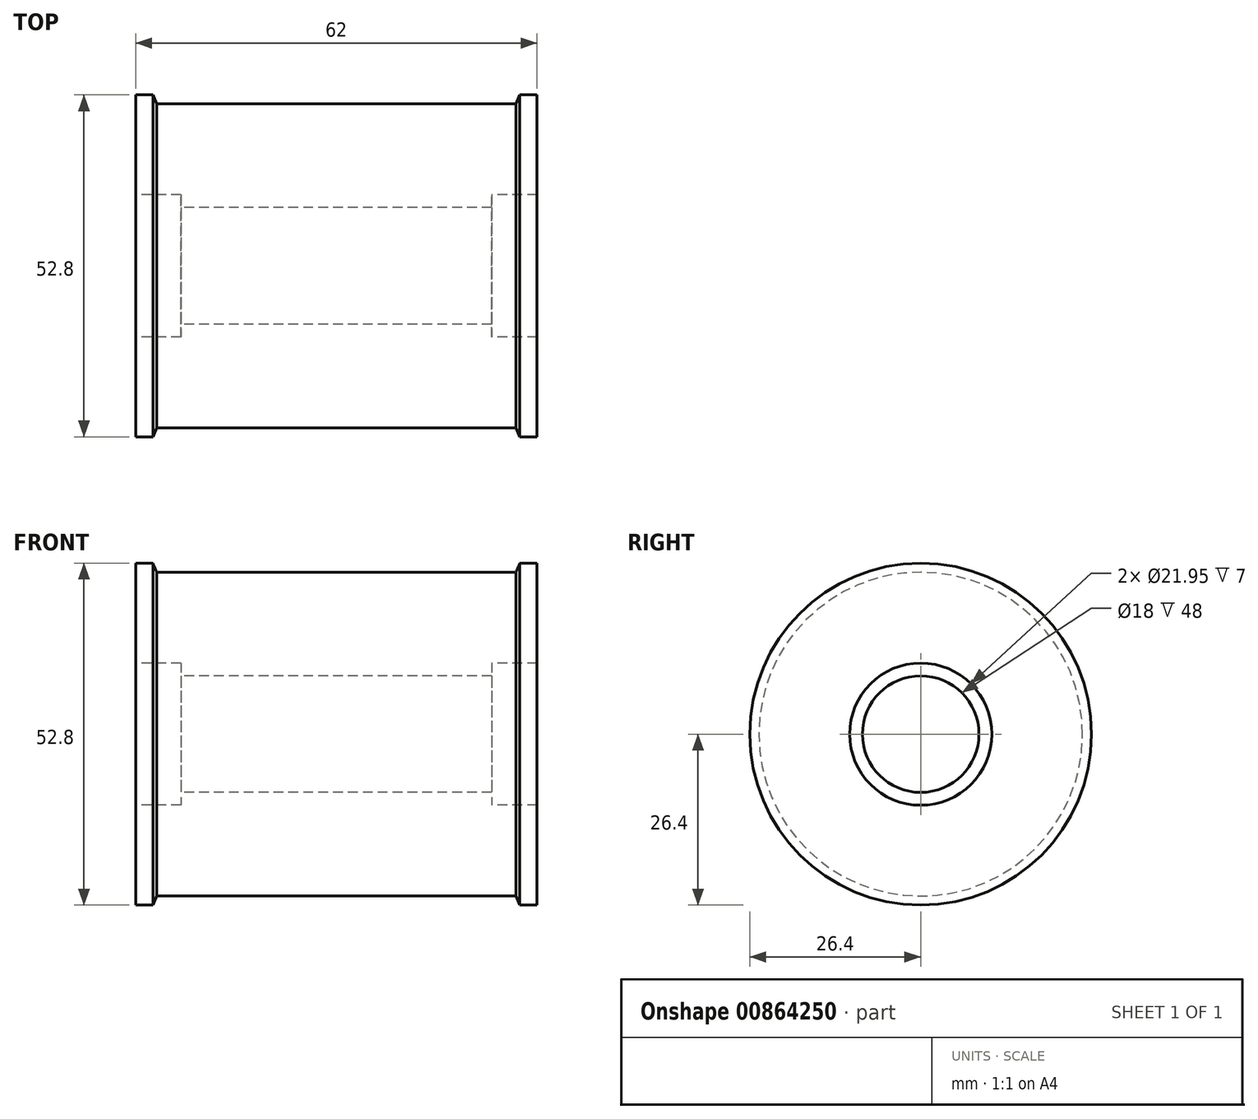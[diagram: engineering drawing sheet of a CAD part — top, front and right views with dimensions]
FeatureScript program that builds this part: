
annotation { "Feature Type Name" : "Feature", "Feature Type Description" : "" }
export const myFeature = defineFeature(function(context is Context, id is Id, definition is map)
    precondition{}
    {
        {
            var Q0;
            Q0=qCreatedBy(makeId("Front.planeOp"),FACE);
            var sketch = newSketch(context, id + "F0", { "sketchPlane" : qUnion([Q0])});
            skLineSegment(sketch, "E0", {"start": v(-4.7, 0) * mm, "end": v(66.37, 0) * mm, "construction": true});
            skLineSegment(sketch, "E1", {"start": v(0, 26.4) * mm, "end": v(0, 10.97) * mm});
            skLineSegment(sketch, "E2", {"start": v(0, 10.97) * mm, "end": v(7, 10.97) * mm});
            skLineSegment(sketch, "E3", {"start": v(7, 10.97) * mm, "end": v(7, 9) * mm});
            skLineSegment(sketch, "E4", {"start": v(7, 9) * mm, "end": v(55, 9) * mm});
            skLineSegment(sketch, "E5", {"start": v(55, 9) * mm, "end": v(55, 10.97) * mm});
            skLineSegment(sketch, "E6", {"start": v(55, 10.97) * mm, "end": v(62, 10.97) * mm});
            skLineSegment(sketch, "E7", {"start": v(62, 10.97) * mm, "end": v(62, 26.4) * mm});
            skLineSegment(sketch, "E8", {"start": v(62, 26.4) * mm, "end": v(59.33, 26.4) * mm});
            skLineSegment(sketch, "E9", {"start": v(2.67, 26.4) * mm, "end": v(3.25, 25) * mm});
            skLineSegment(sketch, "E10", {"start": v(3.25, 25) * mm, "end": v(58.75, 25) * mm});
            skLineSegment(sketch, "E11", {"start": v(58.75, 25) * mm, "end": v(59.33, 26.4) * mm});
            skLineSegment(sketch, "E12.trimOffspring", {"start": v(2.67, 26.4) * mm, "end": v(0, 26.4) * mm});
            skSolve(sketch);
        }
        {
            var Q0;
            Q0 = qSketchRegion(id + "F0", true);
            var Q1;
            Q1=sQuery(id+"F0.wireOp",EDGE,"E0");
            revolve(context, id + "F1", {"surfaceOperationType" : NewSurfaceOperationType.NEW, "entities" : qUnion([Q0]), "axis" : qUnion([Q1]), "revolveType" : RevolveType.FULL});
        }
    });
